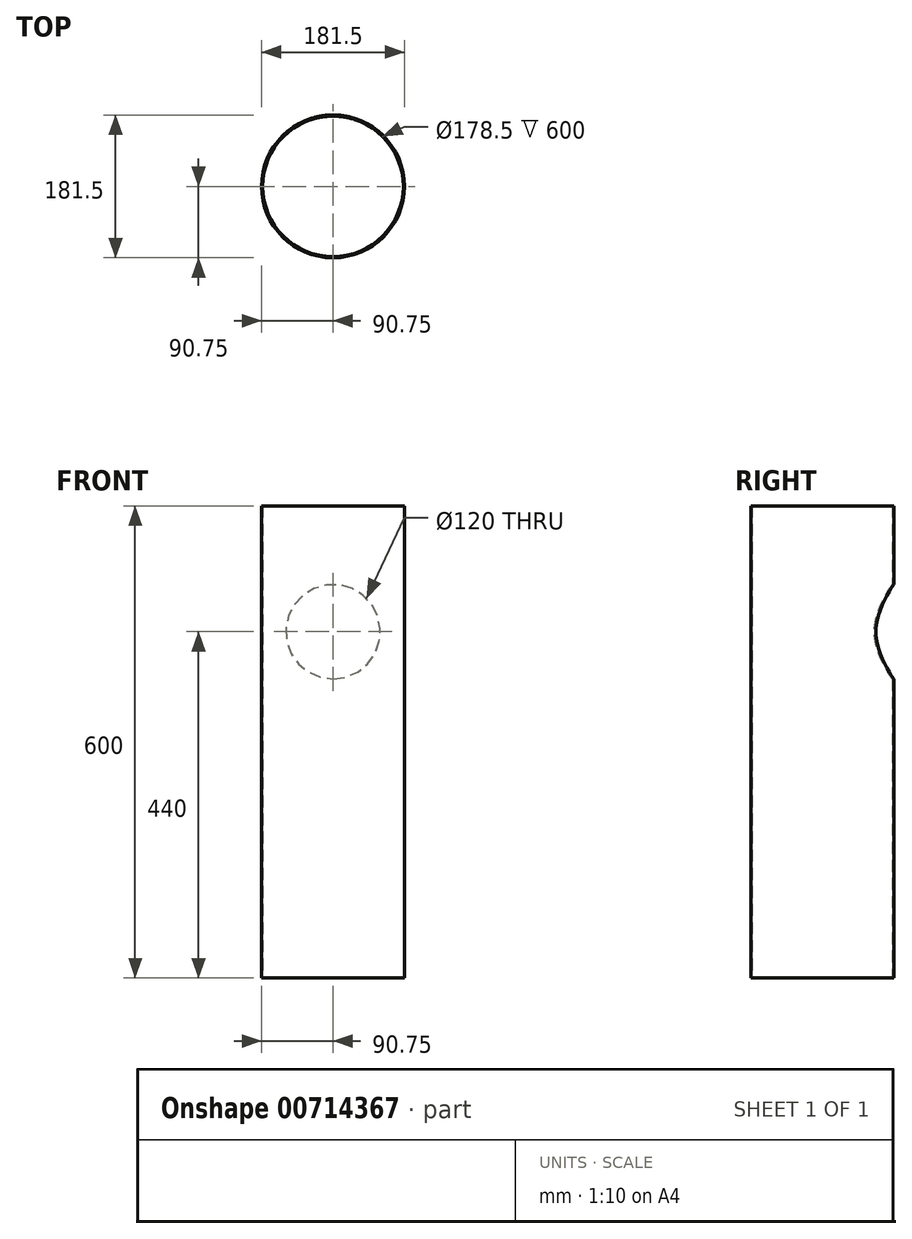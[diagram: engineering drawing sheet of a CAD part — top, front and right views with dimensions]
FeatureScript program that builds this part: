
annotation { "Feature Type Name" : "Feature", "Feature Type Description" : "" }
export const myFeature = defineFeature(function(context is Context, id is Id, definition is map)
    precondition{}
    {
        {
            var Q0;
            Q0=qCreatedBy(makeId("Top.planeOp"),FACE);
            var sketch = newSketch(context, id + "F0", { "sketchPlane" : qUnion([Q0])});
            skCircle(sketch, "E0", {"center": v(0, 0) * mm, "radius": 90.75 * mm});
            skCircle(sketch, "E1.0", {"center": v(0, 0) * mm, "radius": 89.25 * mm});
            skSolve(sketch);
        }
        {
            var Q0;
            Q0=makeQuery(id+"F0.imprint","IMPRINT",FACE,{"disambiguationData":[TD([[makeQuery(id+"F0.imprint","IMPRINT",EDGE,{"derivedFrom":sQuery(id+"F0.wireOp",EDGE,"E0")}),1.0]])]});
            extrude(context, id + "F1", {"entities" : qUnion([Q0]), "depth" : 600 * mm, "offsetDistance" : 25 * mm});
        }
        {
            var Q0;
            Q0=qCreatedBy(makeId("Front.planeOp"),FACE);
            var sketch = newSketch(context, id + "F2", { "sketchPlane" : qUnion([Q0])});
            skCircle(sketch, "E2", {"center": v(0, 440) * mm, "radius": 60 * mm});
            skSolve(sketch);
        }
        {
            var Q0;
            Q0 = qSketchRegion(id + "F2", true);
            extrude(context, id + "F3", {"entities" : qUnion([Q0]), "operationType" : NewBodyOperationType.REMOVE, "oppositeDirection" : true, "depth" : 200 * mm, "offsetDistance" : 25 * mm});
        }
    });
